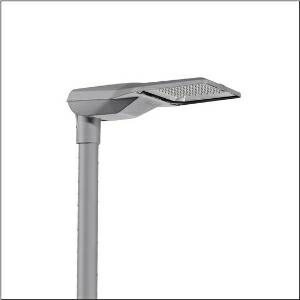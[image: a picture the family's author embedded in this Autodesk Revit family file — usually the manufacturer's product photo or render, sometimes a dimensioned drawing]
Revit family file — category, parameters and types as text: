
# Revit family: streetlight_sl_21_iq_midi___st0_8a_5xe3c31d08mb_7ea8
name_source: partatom
category: Lighting Fixtures
units: mm (PartAtom-declared; Revit-internal decimal feet)

## family parameters
Cut with Voids When Loaded = No
Host = Face
Light Source = No
Part Type = Normal
Room Calculation Point = No
Round Connector Dimension = Use Diameter
Shared = No

## types (1)
- --- (1 x LED, 19500 lm, 146.7 W, 3000K)
    Apparent Load = 147 VA
    CIE Flux Codes = 38 75 97 100 100
    Color Rendering = 70
    Color Temperature = 3000K
    Default Elevation = 1800 mm
    Description = Streetlight SL 21 iQ midi, mast luminaire, primary light control with lens, of PMMA, primary optical cover: cover, of toughened safety glass, transparent, light distribution: ST0.8a, light emission: direct distribution, primary light characteristic: asymmetric, installation type: post-top, side-entry, LED, High Power LED, rated luminous flux: 19.500lm, luminous efficacy: 133lm/W, light colour: 730, colour temperature: 3000K, control gear: iQ-Comfort, control: Auto-Match, Temp-Guard, Lumen-Switch, Night-Set, Smart-Wire, Light-Fading, Desk-Remote (wireless, voltage-free reading and setting of iQ features in the workshop via application-optimized NFC function/RFID function), optimised constant luminous flux control (CLO 2.0), pre-setting: linear dimming characteristic, mains connection: 230..240V, AC, 50/60Hz, start of lifetime: 147W, end of service life: 161W, reduction: 62W, luminaire housing, of diecast aluminium, powder-coated, SITECO metallic grey (DB 702S), corrosivity category C5 high according to DIN EN ISO 12944, please order mast flange separately, inclination adjustable: 0°, 5°, 10°, 15°, sealing non-destructively replaceable, multi-level sealing system, length: 644mm, width: 335mm, height: 110mm, mast flange for spigot size: 42mm (side-entry): 5XC10008XM4, 60/48mm (side-entry/post-top): 5XC10108XM2, 76/60mm (side-entry/post-top): 5XC10108XM1, mounting height: 4..8m, protection rating (complete): IP66, insulation class (complete): insulation class II (safety insulation), certification: CE, ENEC, ENEC+, VDE, impact resistance: IK10, permissible operating ambient temperature for outdoor applications: -40..+50°C, standard-compliant lighting for roads and squares, packaging unit: 1 piece

Light Distribution: ST0.8a
    Height = 111 mm
    Lamp = 1 x LED
    Lamp Light Flux = 19500 lm
    Lamp Power = 146.7 W
    Lamp count = 1
    Length = 644 mm
    Luminous efficacy = 133 lm/W
    Manufacturer = Siteco
    ModVariant = No
    Model = 5XE3C31D08MB
    Number of Poles = 1
    OnlyDefault = Yes
    Power Factor = 1
    Product Name = Streetlight SL 21 iQ midi | ST0.8a
    Product group = mast luminaire | pylon top
    ProductGroupID = 6100
    Protection Class = Protection class II
    Protection Degree = IP 66
    RLX_Detail_Level = 1
    RLX_Emergency_Light_Flux = 0 lm
    RLX_Emergency_Type = 0
    RLX_Emergency_Type_DB = No
    RlxData = <blob elided: 27013 chars, md5=894a1783>
    Socket = socket
    Standby Power = 0 W
    System Light Flux = 19499 lm
    System Power = 147 W
    Type Comments = factory setting: luminous flux: 100 % | dim-lin: 254 | 753 mA
    Type Image = l_1004298.jpg
    URL = http://relux.com
    VarID = @adj_183721
    Voltage = 0 V
    Weight = 0.00 kg
    Width = 336 mm

## geometry (parser evidence)
native form markers: Blend x4, Sweep x12
no freeform markers — native parametric forms only
